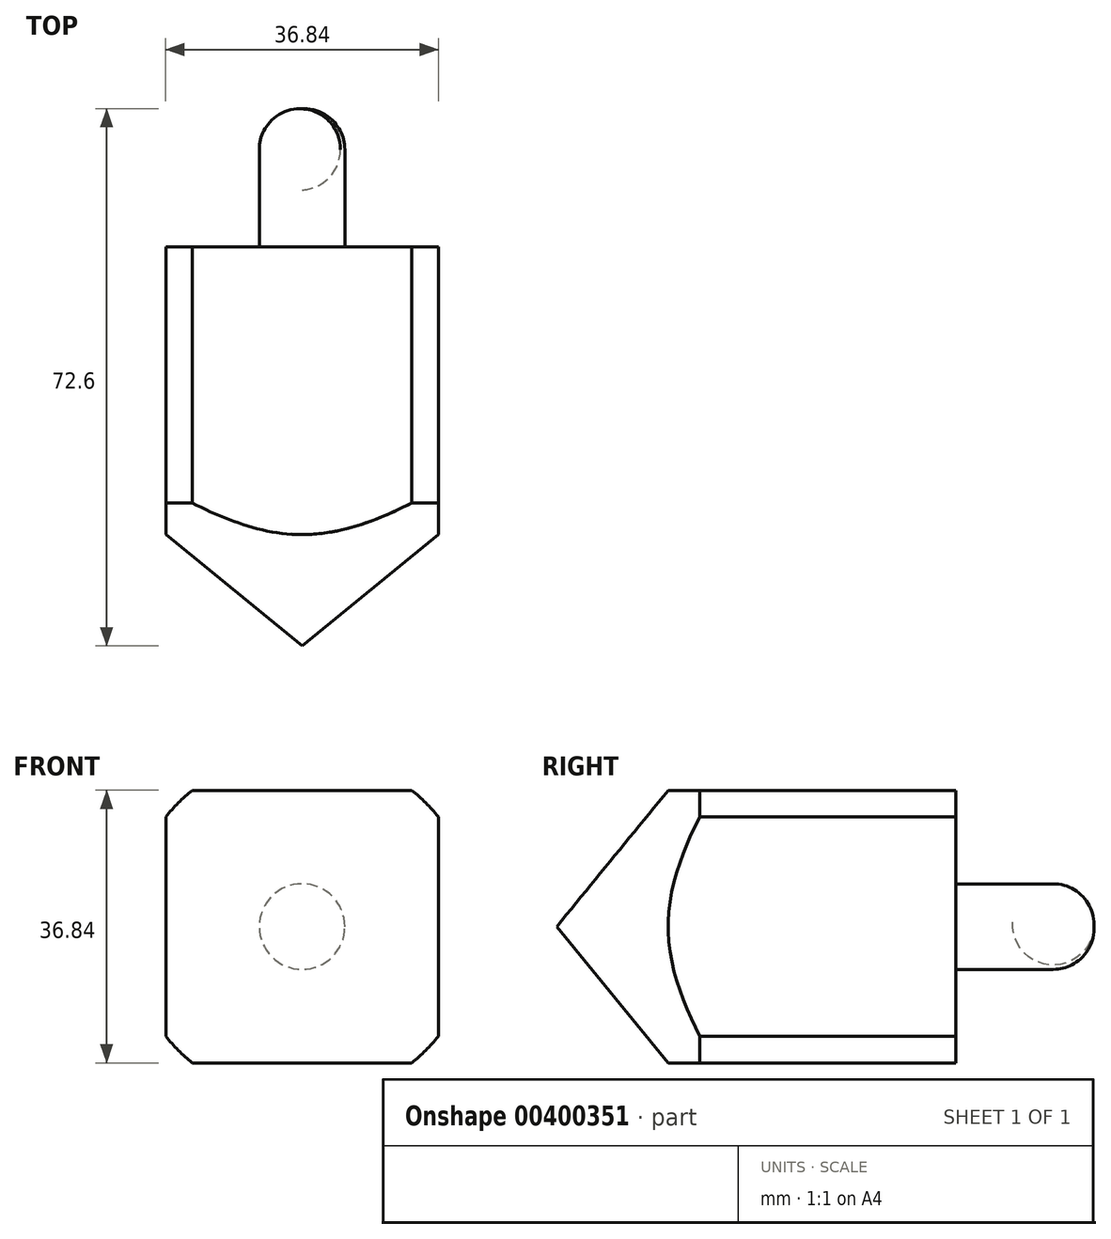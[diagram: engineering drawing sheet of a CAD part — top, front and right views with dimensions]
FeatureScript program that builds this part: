
annotation { "Feature Type Name" : "Feature", "Feature Type Description" : "" }
export const myFeature = defineFeature(function(context is Context, id is Id, definition is map)
    precondition{}
    {
        {
            var Q0;
            Q0=qCreatedBy(makeId("Top.planeOp"),FACE);
            var sketch = newSketch(context, id + "F0", { "sketchPlane" : qUnion([Q0])});
            skLineSegment(sketch, "E0", {"start": v(-5.78, 53.93) * mm, "end": v(-23.65, 53.93) * mm});
            skLineSegment(sketch, "E1", {"start": v(23.06, 54.16) * mm, "end": v(5.2, 54.16) * mm});
            skLineSegment(sketch, "E2", {"start": v(-23.65, 53.93) * mm, "end": v(-23.65, 19.34) * mm});
            skLineSegment(sketch, "E3", {"start": v(23.25, 53.93) * mm, "end": v(23.25, 19.34) * mm});
            skLineSegment(sketch, "E4", {"start": v(-23.65, 19.34) * mm, "end": v(0, 0) * mm});
            skLineSegment(sketch, "E5", {"start": v(0, 0) * mm, "end": v(23.25, 19.34) * mm});
            skLineSegment(sketch, "E6", {"start": v(0, 67.85) * mm, "end": v(0, 0) * mm});
            skLineSegment(sketch, "E7", {"start": v(-5.78, 53.93) * mm, "end": v(-5.78, 67.1) * mm});
            skLineSegment(sketch, "E8", {"start": v(5.2, 54.16) * mm, "end": v(5.2, 67.1) * mm});
            skArc(sketch, "E9", {"start": v(5.2, 67.1) * mm, "mid": v(-0.3, 72.6) * mm, "end": v(-5.78, 67.1) * mm});
            skLineSegment(sketch, "E10", {"start": v(0, 72.6) * mm, "end": v(0, 67.85) * mm});
            skPoint(sketch, "E10.startSnap0", {"position": v(-0.3, 72.6) * mm});
            skSolve(sketch);
        }
        {
            var Q0;
            Q0 = qSketchRegion(id + "F0", true);
            var Q1;
            Q1=sQuery(id+"F0.wireOp",EDGE,"E6");
            revolve(context, id + "F1", {"entities" : qUnion([Q0]), "axis" : qUnion([Q1]), "revolveType" : RevolveType.FULL});
        }
        {
            var Q0;
            Q0=qCreatedBy(makeId("Front.planeOp"),FACE);
            var sketch = newSketch(context, id + "F2", { "sketchPlane" : qUnion([Q0])});
            skLineSegment(sketch, "E11.bottom", {"start": v(18.41, 18.41) * mm, "end": v(-18.41, 18.41) * mm});
            skLineSegment(sketch, "E11.top", {"start": v(18.41, -18.41) * mm, "end": v(-18.41, -18.41) * mm});
            skLineSegment(sketch, "E11.left", {"start": v(18.41, 18.41) * mm, "end": v(18.41, -18.41) * mm});
            skLineSegment(sketch, "E11.right", {"start": v(-18.41, 18.41) * mm, "end": v(-18.41, -18.41) * mm});
            skPoint(sketch, "E11.middle", {"position": v(0, 0) * mm});
            skLineSegment(sketch, "E12.bottom", {"start": v(41.54, 38.26) * mm, "end": v(-41.54, 38.26) * mm});
            skLineSegment(sketch, "E12.top", {"start": v(41.54, -38.26) * mm, "end": v(-41.54, -38.26) * mm});
            skLineSegment(sketch, "E12.left", {"start": v(41.54, 38.26) * mm, "end": v(41.54, -38.26) * mm});
            skLineSegment(sketch, "E12.right", {"start": v(-41.54, 38.26) * mm, "end": v(-41.54, -38.26) * mm});
            skSolve(sketch);
        }
        {
            var Q0;
            Q0=makeQuery(id+"F2.imprint","IMPRINT",FACE,{"disambiguationData":[TD([[makeQuery(id+"F2.imprint","IMPRINT",EDGE,{"derivedFrom":sQuery(id+"F2.wireOp",EDGE,"E11.bottom")}),-1.0]])]});
            extrude(context, id + "F3", {"entities" : qUnion([Q0]), "operationType" : NewBodyOperationType.REMOVE, "oppositeDirection" : true, "depth" : 81.53 * mm});
        }
    });
